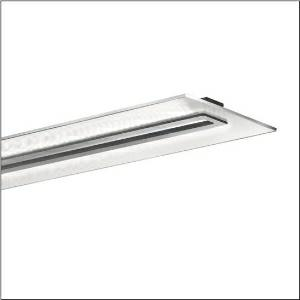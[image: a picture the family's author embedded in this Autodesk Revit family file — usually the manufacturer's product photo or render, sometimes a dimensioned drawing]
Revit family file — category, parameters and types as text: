
# Revit family: vega_r__11_5mn238dle_9bfa
name_source: partatom
category: Lighting Fixtures
units: mm (PartAtom-declared; Revit-internal decimal feet)

## family parameters
Cut with Voids When Loaded = No
Host = Face
Light Source = No
Part Type = Normal
Room Calculation Point = No
Round Connector Dimension = Use Diameter
Shared = No

## types (1)
- --- (1 x LED 4000K / CRI = 80 (unbekannt), 8130 lm, 4000K)
    Apparent Load = 62 VA
    CIE Flux Codes = 61 86 97 62 100
    Color Rendering = 80
    Color Temperature = 4000K
    Default Elevation = 1800 mm
    Description = Vega® 11, office luminaire, primary light control with prismatic reflector, of PMMA, transparent prismatic structure, CAT 2 (L<= 1500cd/m²), light emission: direct/indirect distribution, primary light characteristic: symmetric, installation type: suspended mounting, surface-mounted, LED, rated luminous flux: 8.130lm, luminous efficacy: 131lm/W, light colour: 840, colour temperature: 4000K, control gear: DALI, with terminal, 3+2-pole, max. 2.5mm², mains connection: 230V, AC, 50Hz, connection cable inclusive, cable length: 1,5m, rated input power: 62W, luminaire housing, rectangular, rounded, of aluminium section, anodised, metallic grey (RAL 9006), length: 1.250mm, width: 350mm, height: 43mm, luminaire housing, lower part, of aluminium section, anodised, metallic grey (RAL 9006), of PC, grey, protection rating (complete): IP20, insulation class (complete): insulation class I (protective earthing), certification: CE, standard: EN 50419, packaging unit: 1 piece
    Height = 40 mm  [stored 0.131234 ft]
    Lamp = 1 x LED 4000K / CRI >= 80 (unbekannt)
    Lamp Light Flux = 8130 lm
    Lamp count = 1
    Length = 1250 mm
    Luminous efficacy = 131 lm/W
    Manufacturer = Siteco
    ModVariant = No
    Model = 5MN238DLE
    Mounting Place = Ceiling
    Mounting Type = Pendant
    Number of Poles = 1
    OnlyDefault = Yes
    Power Factor = 1
    Product Name = Vega® 11
    Product group = office luminaire | ceiling pendant
    ProductGroupID = 903
    Protection Class = Protection class I
    Protection Degree = IP 20
    RLX_Detail_Level = 1
    RLX_Emergency_Light_Flux = 0 lm
    RLX_Emergency_Type = 0
    RLX_Emergency_Type_DB = No
    RlxData = <blob elided: 62833 chars, md5=2ab0f590>
    Socket = socket
    Standby Power = 0 W
    System Light Flux = 8130 lm
    System Power = 62 W
    Type Comments = factory setting: luminous flux: 100 % | dim-lin: 254 | 458 mA
    Type Image = l_1004807.jpg
    URL = http://relux.com
    VarID = @adj_221001
    Voltage = 0 V
    Weight = 0.00 kg
    Width = 350 mm

note: [stored X ft] marks values corroborated as IEEE doubles in the binary element streams (Revit-internal decimal feet)

## geometry (parser evidence)
native form markers: Blend x4, Sweep x11
no freeform markers — native parametric forms only
